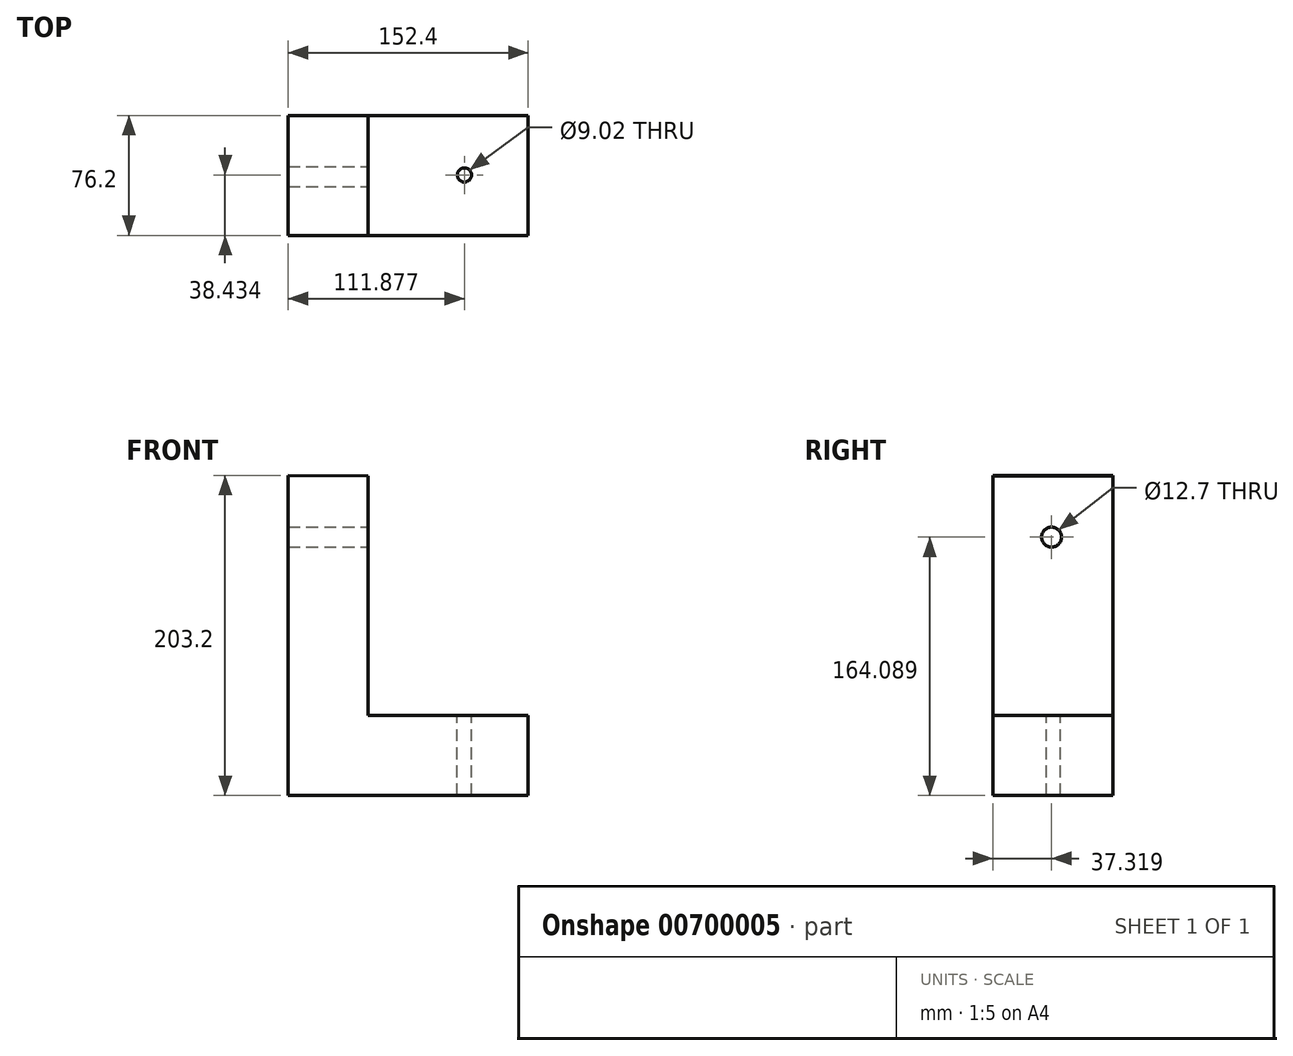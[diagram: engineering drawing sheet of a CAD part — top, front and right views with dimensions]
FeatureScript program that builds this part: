
annotation { "Feature Type Name" : "Feature", "Feature Type Description" : "" }
export const myFeature = defineFeature(function(context is Context, id is Id, definition is map)
    precondition{}
    {
        {
            var Q0;
            Q0=qCreatedBy(makeId("Front.planeOp"),FACE);
            var sketch = newSketch(context, id + "F0", { "sketchPlane" : qUnion([Q0])});
            skLineSegment(sketch, "E0", {"start": v(-96.84, 105.44) * mm, "end": v(-96.84, -97.76) * mm});
            skLineSegment(sketch, "E1", {"start": v(-96.84, -97.76) * mm, "end": v(55.56, -97.76) * mm});
            skLineSegment(sketch, "E2", {"start": v(55.56, -97.76) * mm, "end": v(55.56, -46.96) * mm});
            skLineSegment(sketch, "E3", {"start": v(55.56, -46.96) * mm, "end": v(-46.04, -46.96) * mm});
            skLineSegment(sketch, "E4", {"start": v(-46.04, -46.96) * mm, "end": v(-46.04, 105.11) * mm});
            skLineSegment(sketch, "E5", {"start": v(-46.04, 105.11) * mm, "end": v(-96.84, 105.44) * mm});
            skSolve(sketch);
        }
        {
            var Q0;
            Q0=makeQuery(id+"F0.imprint","IMPRINT",FACE,{"disambiguationData":[TD([[makeQuery(id+"F0.imprint","IMPRINT",EDGE,{"derivedFrom":sQuery(id+"F0.wireOp",EDGE,"E0")}),1.0]])]});
            extrude(context, id + "F1", {"entities" : qUnion([Q0]), "depth" : 76.2 * mm, "offsetDistance" : 25.4 * mm});
        }
        {
            var Q0;
            Q0=makeQuery(id+"F1.opExtrude","SWEPT_FACE",FACE,{"disambiguationData":[OSD([sQuery(id+"F0.wireOp",EDGE,"E3")])]});
            var sketch = newSketch(context, id + "F2", { "sketchPlane" : qUnion([Q0])});
            skCircle(sketch, "E6", {"center": v(15.04, -37.77) * mm, "radius": 4.5 * mm});
            skSolve(sketch);
        }
        {
            var Q0;
            Q0=makeQuery(id+"F2.imprint","IMPRINT",FACE,{"disambiguationData":[TD([[makeQuery(id+"F2.imprint","IMPRINT",EDGE,{"derivedFrom":sQuery(id+"F2.wireOp",EDGE,"E6")}),1.0]])]});
            extrude(context, id + "F3", {"entities" : qUnion([Q0]), "operationType" : NewBodyOperationType.REMOVE, "oppositeDirection" : true, "depth" : 92.76 * mm, "offsetDistance" : 25.4 * mm});
        }
        {
            var Q0;
            Q0=makeQuery(id+"F1.opExtrude","SWEPT_FACE",FACE,{"disambiguationData":[OSD([sQuery(id+"F0.wireOp",EDGE,"E4")])]});
            var sketch = newSketch(context, id + "F4", { "sketchPlane" : qUnion([Q0])});
            skCircle(sketch, "E7", {"center": v(-38.88, 66.33) * mm, "radius": 6.35 * mm});
            skSolve(sketch);
        }
        {
            var Q0;
            Q0=makeQuery(id+"F4.imprint","IMPRINT",FACE,{"disambiguationData":[TD([[makeQuery(id+"F4.imprint","IMPRINT",EDGE,{"derivedFrom":sQuery(id+"F4.wireOp",EDGE,"E7")}),1.0]])]});
            extrude(context, id + "F5", {"entities" : qUnion([Q0]), "operationType" : NewBodyOperationType.REMOVE, "oppositeDirection" : true, "depth" : 118.67 * mm, "offsetDistance" : 25.4 * mm});
        }
    });
